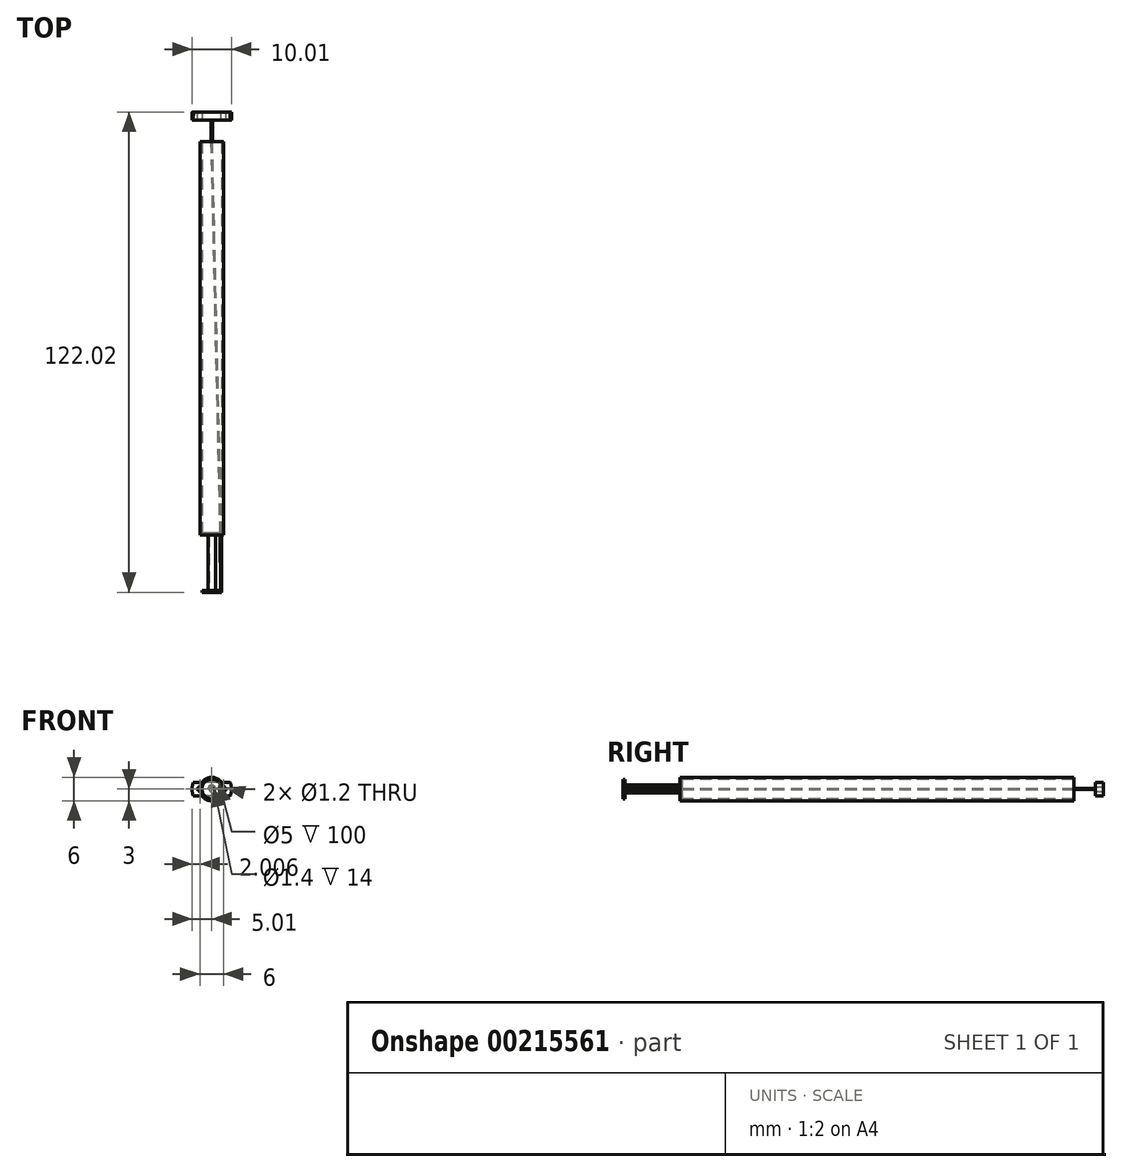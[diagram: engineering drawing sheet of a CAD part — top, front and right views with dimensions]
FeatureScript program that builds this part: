
annotation { "Feature Type Name" : "Feature", "Feature Type Description" : "" }
export const myFeature = defineFeature(function(context is Context, id is Id, definition is map)
    precondition{}
    {
        {
            var Q0;
            Q0=qCreatedBy(makeId("Front.planeOp"),FACE);
            var sketch = newSketch(context, id + "F0", { "sketchPlane" : qUnion([Q0])});
            skLineSegment(sketch, "E0", {"start": v(0, 0) * mm, "end": v(0, 2.72) * mm, "construction": true});
            skLineSegment(sketch, "E1", {"start": v(-2.72, 0) * mm, "end": v(0, 0) * mm, "construction": true});
            skPoint(sketch, "E2.right.start.orphan", {"position": v(2.72, 2.72) * mm});
            skPoint(sketch, "E3.orphan", {"position": v(-2.72, -2.72) * mm});
            skPoint(sketch, "E2.left.start.orphan", {"position": v(-2.72, 2.72) * mm});
            skPoint(sketch, "E4.center.orphan", {"position": v(2.72, 0) * mm});
            skPoint(sketch, "E5.trimOffspring.end.orphan", {"position": v(2.72, -2.72) * mm});
            skLineSegment(sketch, "E6", {"start": v(2.45, -0.5) * mm, "end": v(2.45, -0.5) * mm});
            skPoint(sketch, "E7.center.orphan", {"position": v(2.5, 0) * mm});
            skCircle(sketch, "E8", {"center": v(0, 0) * mm, "radius": 2.5 * mm});
            skSolve(sketch);
        }
        {
            var Q0;
            Q0 = qSketchRegion(id + "F0", true);
            extrude(context, id + "F1", {"entities" : qUnion([Q0]), "depth" : 0.5 * mm});
        }
        {
            var Q0;
            Q0=makeQuery(id+"F1.opExtrude","CAP_FACE",FACE,{"disambiguationData":[OSD([sQuery(id+"F0.wireOp",EDGE,"E8")])],"isStart":true});
            var sketch = newSketch(context, id + "F2", { "sketchPlane" : qUnion([Q0])});
            skCircle(sketch, "E9", {"center": v(0, 0) * mm, "radius": 0.7 * mm});
            skCircle(sketch, "E10", {"center": v(0, 0) * mm, "radius": 1 * mm});
            skSolve(sketch);
        }
        {
            var Q0;
            Q0 = qSketchRegion(id + "F2", true);
            extrude(context, id + "F3", {"entities" : qUnion([Q0]), "operationType" : NewBodyOperationType.ADD, "depth" : 14 * mm});
        }
        {
            var Q0;
            Q0=makeQuery(id+"F3.opExtrude","CAP_FACE",FACE,{"disambiguationData":[OSD([sQuery(id+"F2.wireOp",EDGE,"E9"),sQuery(id+"F2.wireOp",EDGE,"E10")])],"isStart":false});
            var sketch = newSketch(context, id + "F4", { "sketchPlane" : qUnion([Q0])});
            skLineSegment(sketch, "E11.0", {"start": v(-2.5, -0.2) * mm, "end": v(-2.5, -0.2) * mm});
            skPoint(sketch, "E12.center.orphan", {"position": v(-2.34, 0) * mm});
            skArc(sketch, "E13.0", {"start": v(-2.5, -0.1) * mm, "mid": v(2.5, 0) * mm, "end": v(-2.5, 0.1) * mm});
            skPoint(sketch, "E14.center.orphan", {"position": v(-2.3, 0) * mm});
            skArc(sketch, "E15", {"start": v(-2.5, -0.1) * mm, "mid": v(-2.08, 0) * mm, "end": v(-2.5, 0.1) * mm});
            skSolve(sketch);
        }
        {
            var Q0;
            Q0 = qSketchRegion(id + "F4", true);
            extrude(context, id + "F5", {"entities" : qUnion([Q0]), "operationType" : NewBodyOperationType.ADD, "depth" : 0.5 * mm});
        }
        {
            var Q0;
            {var subQ0=sQuery(id+"F0.wireOp",EDGE,"E8");Q0=makeQuery(id+"F3.boolean.opBoolean","SPLIT",FACE,{"disambiguationData":[TD([makeQuery(id+"F1.opExtrude","SWEPT_FACE",FACE,{"disambiguationData":[OSD([subQ0])]})])],"derivedFrom":makeQuery(id+"F1.opExtrude","CAP_FACE",FACE,{"disambiguationData":[OSD([subQ0])],"isStart":true})});}
            var sketch = newSketch(context, id + "F6", { "sketchPlane" : qUnion([Q0])});
            skCircle(sketch, "E16", {"center": v(-2.35, 0) * mm, "radius": 0.15 * mm});
            skSolve(sketch);
        }
        {
            var Q0;
            {var subQ0=sQuery(id+"F4.wireOp",EDGE,"E13.0");var subQ1=sQuery(id+"F4.wireOp",EDGE,"E15");Q0=makeQuery(id+"F5.boolean.opBoolean","SPLIT",FACE,{"disambiguationData":[TD([makeQuery(id+"F3.opExtrude","SWEPT_FACE",FACE,{"disambiguationData":[OSD([sQuery(id+"F2.wireOp",EDGE,"E10")])]})])],"derivedFrom":makeQuery(id+"F5.opExtrude","CAP_FACE",FACE,{"disambiguationData":[OSD([subQ0,subQ1])],"isStart":true})});}
            var sketch = newSketch(context, id + "F7", { "sketchPlane" : qUnion([Q0])});
            skCircle(sketch, "E17", {"center": v(0, 0) * mm, "radius": 3 * mm});
            skCircle(sketch, "E18", {"center": v(0, 0) * mm, "radius": 2.5 * mm});
            skSolve(sketch);
        }
        {
            var Q0;
            Q0=qCreatedBy(makeId("Top.planeOp"),FACE);
            var sketch = newSketch(context, id + "F8", { "sketchPlane" : qUnion([Q0])});
            skPoint(sketch, "E19.0", {"position": v(2.35, 0) * mm});
            skLineSegment(sketch, "E20.0", {"start": v(2.5, 14.5) * mm, "end": v(2.08, 14.5) * mm, "construction": true});
            skLineSegment(sketch, "E21", {"start": v(2.29, 14.5) * mm, "end": v(2.35, 0) * mm});
            skLineSegment(sketch, "E22", {"start": v(0, 0) * mm, "end": v(0, 115) * mm, "construction": true});
            skLineSegment(sketch, "E23", {"start": v(0, 115) * mm, "end": v(2.29, 14.5) * mm});
            skPoint(sketch, "E24.visualSharp", {"position": v(2.29, 14.5) * mm});
            skArc(sketch, "E24.filletArc", {"start": v(2.29, 14.5) * mm, "mid": v(2.29, 14.5) * mm, "end": v(2.29, 14.5) * mm});
            skLineSegment(sketch, "E25", {"start": v(0, 115) * mm, "end": v(0, 121.5) * mm});
            skPoint(sketch, "E26.visualSharp", {"position": v(0, 115) * mm});
            skArc(sketch, "E26.filletArc", {"start": v(0, 115) * mm, "mid": v(0, 115) * mm, "end": v(0, 115) * mm});
            skSolve(sketch);
        }
        {
            var Q0;
            Q0=makeQuery(id+"F6.imprint","IMPRINT",FACE,{"disambiguationData":[TD([[makeQuery(id+"F6.imprint","IMPRINT",EDGE,{"derivedFrom":sQuery(id+"F6.wireOp",EDGE,"E16")}),1.0]])]});
            var Q1;
            Q1=sQuery(id+"F8.wireOp",EDGE,"E21");
            var Q2;
            Q2=sQuery(id+"F8.wireOp",EDGE,"E24.filletArc");
            var Q3;
            Q3=sQuery(id+"F8.wireOp",EDGE,"E23");
            var Q4;
            Q4=sQuery(id+"F8.wireOp",EDGE,"E26.filletArc");
            var Q5;
            Q5=sQuery(id+"F8.wireOp",EDGE,"E25");
            sweep(context, id + "F9", {"operationType" : NewBodyOperationType.ADD, "profiles" : qUnion([Q0]), "path" : qUnion([Q1, Q2, Q3, Q4, Q5])});
        }
        {
            var Q0;
            Q0=makeQuery(id+"F7.imprint","IMPRINT",FACE,{"disambiguationData":[TD([[makeQuery(id+"F7.imprint","IMPRINT",EDGE,{"derivedFrom":sQuery(id+"F7.wireOp",EDGE,"E17")}),1.0]])]});
            extrude(context, id + "F10", {"entities" : qUnion([Q0]), "operationType" : NewBodyOperationType.ADD, "oppositeDirection" : true, "depth" : 100 * mm});
        }
        {
            var Q0;
            Q0=makeQuery(id+"F9.opSweep","CAP_FACE",FACE,{"disambiguationData":[OSD([sQuery(id+"F6.wireOp",EDGE,"E16"),sQuery(id+"F8.wireOp",VERTEX,"E25.end")])],"isStart":false});
            var sketch = newSketch(context, id + "F11", { "sketchPlane" : qUnion([Q0])});
            skArc(sketch, "E27", {"start": v(-4.15, 1.75) * mm, "mid": v(-4.47, 0) * mm, "end": v(-4.15, -1.75) * mm});
            skCircle(sketch, "E28", {"center": v(-2.47, 0) * mm, "radius": 0.6 * mm});
            skCircle(sketch, "E29", {"center": v(3.53, 0) * mm, "radius": 0.6 * mm});
            skLineSegment(sketch, "E30.bottom", {"start": v(-4.15, 1.75) * mm, "end": v(5.22, 1.75) * mm});
            skLineSegment(sketch, "E30.top", {"start": v(-4.15, -1.75) * mm, "end": v(5.22, -1.75) * mm});
            skLineSegment(sketch, "E31", {"start": v(0.53, 0) * mm, "end": v(7.91, 0) * mm, "construction": true});
            skPoint(sketch, "E32.orphan", {"position": v(7.91, 1.75) * mm});
            skPoint(sketch, "E33.orphan", {"position": v(7.91, -1.75) * mm});
            skArc(sketch, "E34.trimOffspring", {"start": v(5.22, -1.75) * mm, "mid": v(5.53, 0) * mm, "end": v(5.22, 1.75) * mm});
            skSolve(sketch);
        }
        {
            var Q0;
            Q0 = qSketchRegion(id + "F11", true);
            extrude(context, id + "F12", {"entities" : qUnion([Q0]), "operationType" : NewBodyOperationType.ADD, "oppositeDirection" : true, "depth" : 2 * mm});
        }
    });
